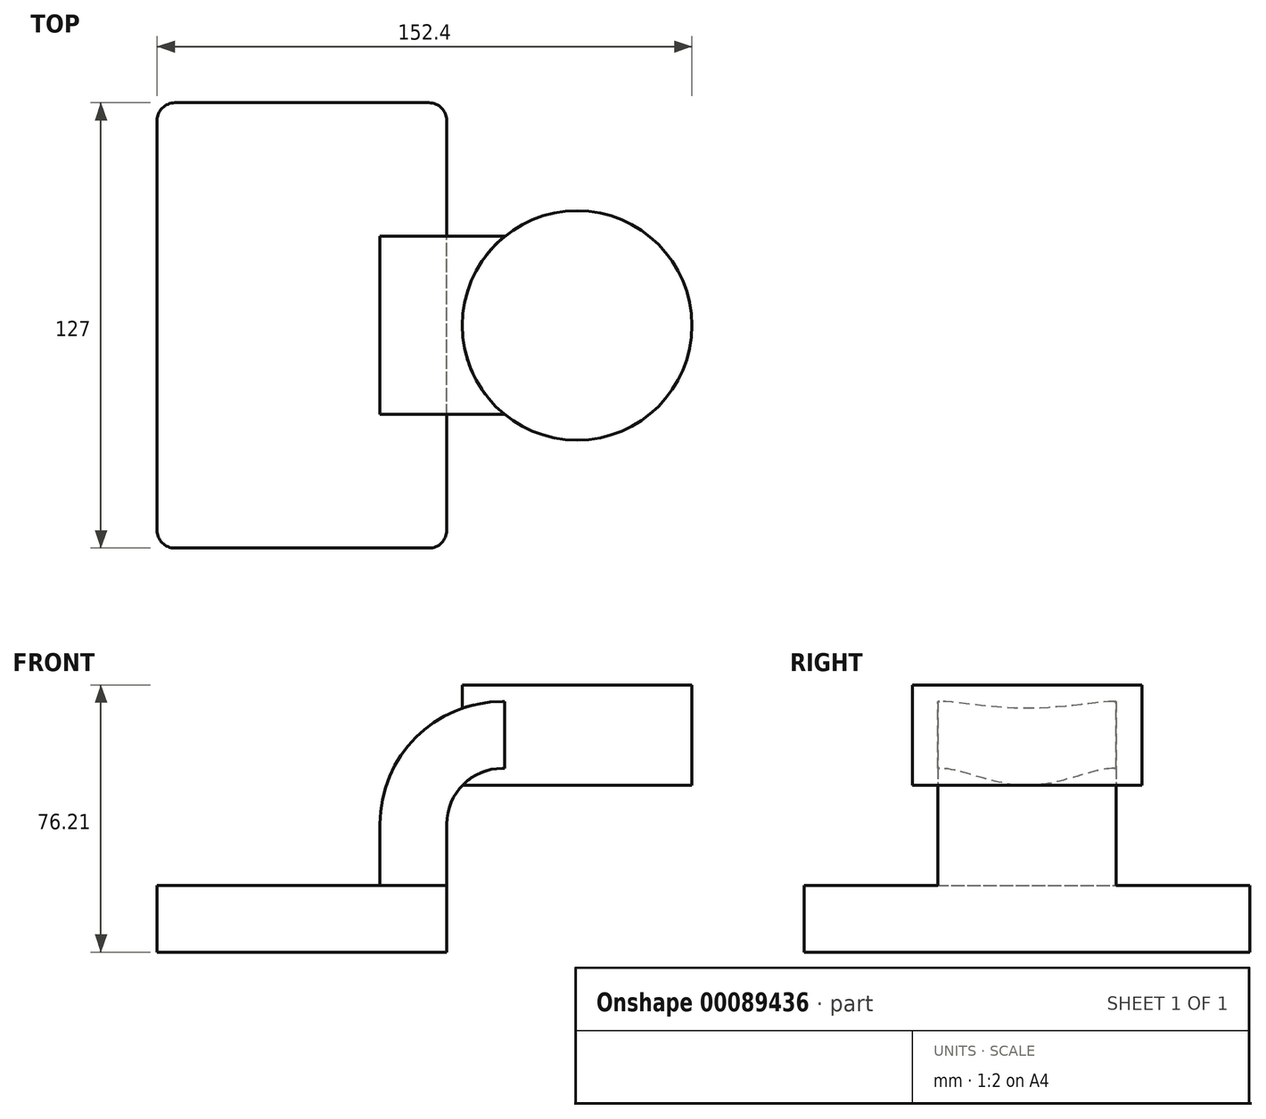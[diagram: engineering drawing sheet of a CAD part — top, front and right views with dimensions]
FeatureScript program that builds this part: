
annotation { "Feature Type Name" : "Feature", "Feature Type Description" : "" }
export const myFeature = defineFeature(function(context is Context, id is Id, definition is map)
    precondition{}
    {
        {
            var Q0;
            Q0=qCreatedBy(makeId("Front.planeOp"),FACE);
            var sketch = newSketch(context, id + "F0", { "sketchPlane" : qUnion([Q0])});
            skLineSegment(sketch, "E0.bottom", {"start": v(41.28, -9.52) * mm, "end": v(-41.27, -9.53) * mm});
            skLineSegment(sketch, "E0.top", {"start": v(41.27, 9.53) * mm, "end": v(-41.28, 9.53) * mm});
            skLineSegment(sketch, "E0.left", {"start": v(41.28, -9.52) * mm, "end": v(41.28, 9.53) * mm});
            skLineSegment(sketch, "E0.right", {"start": v(-41.27, -9.53) * mm, "end": v(-41.28, 9.53) * mm});
            skPoint(sketch, "E0.middle", {"position": v(0, 0) * mm});
            skLineSegment(sketch, "E1.bottom", {"start": v(111.12, 38.1) * mm, "end": v(60.32, 38.1) * mm});
            skLineSegment(sketch, "E1.top", {"start": v(111.12, 66.68) * mm, "end": v(60.32, 66.68) * mm});
            skLineSegment(sketch, "E1.left", {"start": v(111.12, 38.1) * mm, "end": v(111.12, 66.68) * mm});
            skLineSegment(sketch, "E1.right", {"start": v(60.32, 38.1) * mm, "end": v(60.32, 66.68) * mm});
            skPoint(sketch, "E1.middle", {"position": v(85.72, 52.39) * mm});
            skLineSegment(sketch, "E2", {"start": v(41.27, 9.53) * mm, "end": v(41.27, 27) * mm});
            skArc(sketch, "E3", {"start": v(41.27, 27) * mm, "mid": v(45.92, 38.23) * mm, "end": v(57.15, 42.88) * mm});
            skLineSegment(sketch, "E4", {"start": v(57.15, 42.88) * mm, "end": v(78.41, 42.88) * mm});
            skLineSegment(sketch, "E5.0", {"start": v(57.15, 61.93) * mm, "end": v(78.41, 61.93) * mm});
            skArc(sketch, "E5.1", {"start": v(22.23, 27) * mm, "mid": v(32.45, 51.7) * mm, "end": v(57.15, 61.93) * mm});
            skLineSegment(sketch, "E5.2", {"start": v(22.22, 9.53) * mm, "end": v(22.22, 27) * mm});
            skLineSegment(sketch, "E6", {"start": v(78.41, 66.68) * mm, "end": v(78.41, 38.1) * mm});
            skFitSpline(sketch, "E7", {"points": [v(-41.28, 9.52) * mm, v(-19.49, 35.95) * mm, v(13.07, 55.57) * mm, v(57.15, 61.93) * mm], "startDerivative": vector(35.34, 88.97) * mm, "endDerivative": vector(124.12, -5.64) * mm});
            skSolve(sketch);
        }
        {
            var Q0;
            Q0=makeQuery(id+"F0.imprint","IMPRINT",FACE,{"disambiguationData":[TD([[makeQuery(id+"F0.imprint","IMPRINT",EDGE,{"derivedFrom":sQuery(id+"F0.wireOp",EDGE,"E0.bottom")}),-1.0]])]});
            extrude(context, id + "F1", {"entities" : qUnion([Q0]), "endBound" : BoundingType.SYMMETRIC, "depth" : 127 * mm});
        }
        {
            var Q0;
            {var subQ1=sQuery(id+"F0.wireOp",EDGE,"E2");Q0=makeQuery(id+"F0.imprint","IMPRINT",FACE,{"disambiguationData":[TD([[makeQuery(id+"F0.imprint","IMPRINT",EDGE,{"derivedFrom":subQ1}),1.0]])]});}
            var Q1;
            {var subQ0=sQuery(id+"F0.wireOp",EDGE,"E4");var subQ1=sQuery(id+"F0.wireOp",EDGE,"E1.right");var subQ2=makeQuery(id+"F0.imprint","INTERSECT",VERTEX,{"derivedFrom":[subQ1,subQ0]});Q1=makeQuery(id+"F0.imprint","IMPRINT",FACE,{"disambiguationData":[TD([[makeQuery(id+"F0.imprint","IMPRINT",EDGE,{"disambiguationData":[TD([[subQ2,-1.0]])],"derivedFrom":subQ1}),-1.0]])]});}
            extrude(context, id + "F2", {"entities" : qUnion([Q0, Q1]), "operationType" : NewBodyOperationType.ADD, "endBound" : BoundingType.SYMMETRIC, "depth" : 50.8 * mm});
        }
        {
            var Q0;
            Q0=makeQuery(id+"F0.imprint","IMPRINT",FACE,{"disambiguationData":[TD([[makeQuery(id+"F0.imprint","IMPRINT",EDGE,{"derivedFrom":sQuery(id+"F0.wireOp",EDGE,"E5.1")}),1.0]])]});
            extrude(context, id + "F3", {"entities" : qUnion([Q0]), "operationType" : NewBodyOperationType.ADD, "endBound" : BoundingType.SYMMETRIC, "depth" : 15.88 * mm});
        }
        {
            var Q0;
            {var subQ0=sQuery(id+"F0.wireOp",EDGE,"E1.left");Q0=makeQuery(id+"F0.imprint","IMPRINT",FACE,{"disambiguationData":[TD([[makeQuery(id+"F0.imprint","IMPRINT",EDGE,{"derivedFrom":subQ0}),1.0]])]});}
            var Q1;
            Q1=sQuery(id+"F0.wireOp",EDGE,"E6");
            revolve(context, id + "F4", {"operationType" : NewBodyOperationType.ADD, "entities" : qUnion([Q0]), "axis" : qUnion([Q1]), "revolveType" : RevolveType.FULL});
        }
        {
            var Q0;
            Q0=makeQuery(id+"F1.opExtrude","CAP_EDGE",EDGE,{"disambiguationData":[OSD([sQuery(id+"F0.wireOp",EDGE,"E0.right")])],"isStart":false});
            var Q1;
            Q1=makeQuery(id+"F1.opExtrude","CAP_EDGE",EDGE,{"disambiguationData":[OSD([sQuery(id+"F0.wireOp",EDGE,"E0.left")])],"isStart":false});
            fillet(context, id + "F5", {"entities" : qUnion([Q0, Q1]), "radius" : 5.08 * mm, "tangentPropagation" : true, "allowEdgeOverflow" : false});
        }
        {
            var Q0;
            Q0=makeQuery(id+"F1.opExtrude","CAP_EDGE",EDGE,{"disambiguationData":[OSD([sQuery(id+"F0.wireOp",EDGE,"E0.left")])],"isStart":true});
            var Q1;
            Q1=makeQuery(id+"F1.opExtrude","CAP_EDGE",EDGE,{"disambiguationData":[OSD([sQuery(id+"F0.wireOp",EDGE,"E0.right")])],"isStart":true});
            fillet(context, id + "F6", {"entities" : qUnion([Q0, Q1]), "radius" : 5.08 * mm, "tangentPropagation" : true, "allowEdgeOverflow" : false});
        }
    });
